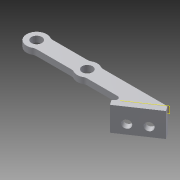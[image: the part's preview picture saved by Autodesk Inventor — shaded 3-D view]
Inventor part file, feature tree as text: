
AUTODESK INVENTOR PART (.ipt)
format: ipt  version: 2014 (Build 180170000, 170)  size: 152,576 bytes
history: native  units: mm
features: other x3, extrude x2, fillet x2, sketch x2
ambient origin geometry x8: Origin, YZ Plane, XZ Plane, XY Plane, X Axis, Y Axis, Z Axis, Center Point
bodies: Body1 (feature_tree)
feature tree (9):
  other  "ソリッド1"
  extrude  "押し出し1"  Depth=4.0mm
  other  "面の勾配1"
  other  "作業平面1"
  extrude  "押し出し3"  Depth=45.0mm
  fillet  "フィレット2"  Radius=5.2mm
  fillet  "フィレット5"  Radius=5.2mm
  sketch  "スケッチ1"
  sketch  "スケッチ3"
